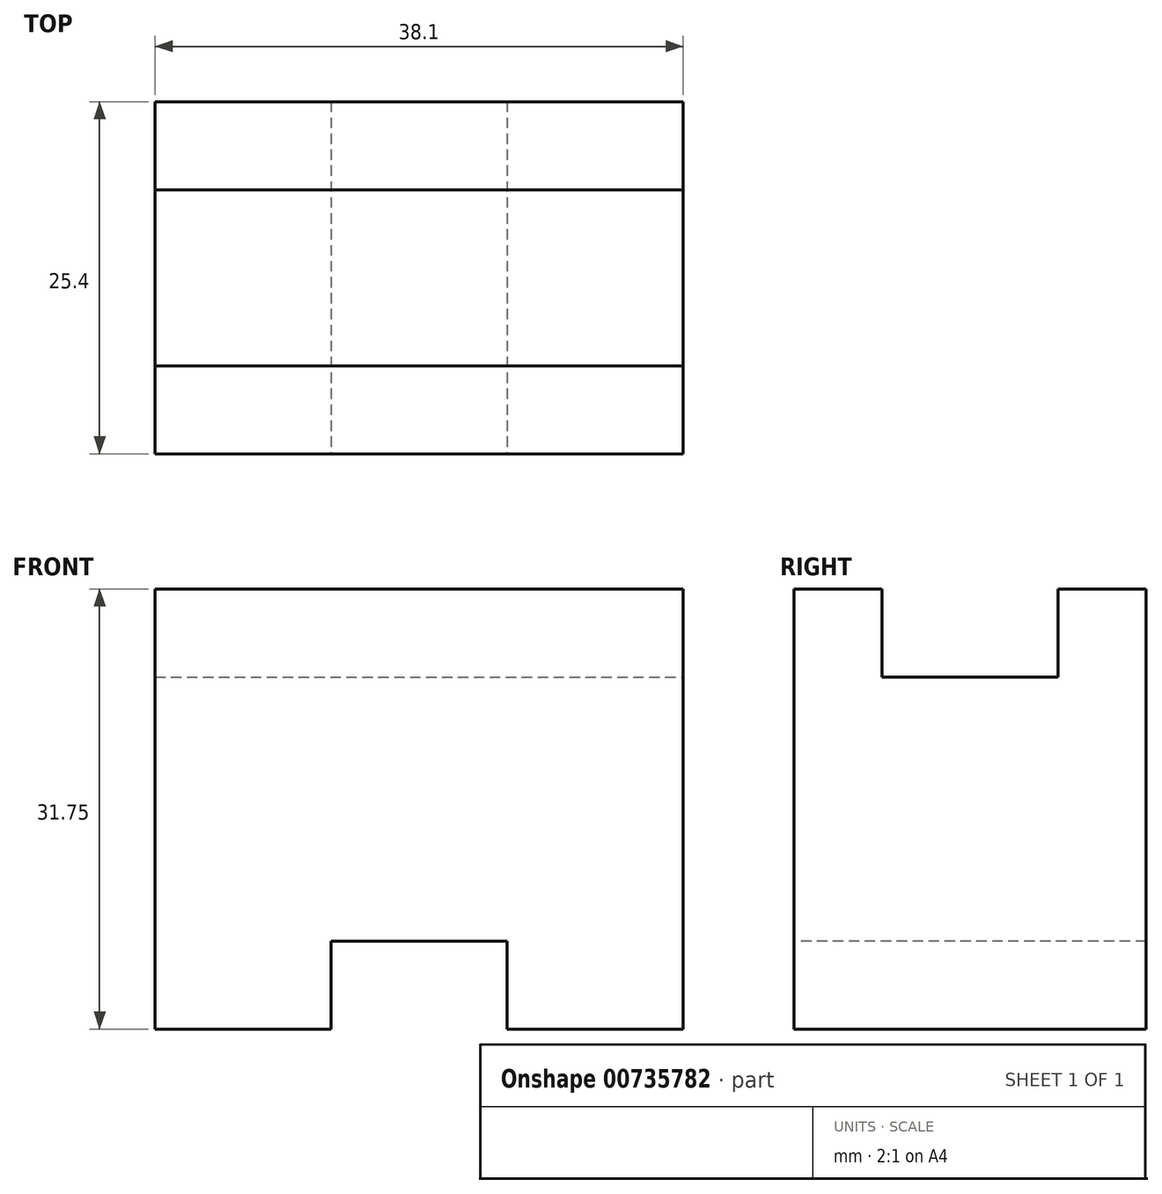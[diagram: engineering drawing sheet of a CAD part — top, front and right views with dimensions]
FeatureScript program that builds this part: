
annotation { "Feature Type Name" : "Feature", "Feature Type Description" : "" }
export const myFeature = defineFeature(function(context is Context, id is Id, definition is map)
    precondition{}
    {
        {
            var Q0;
            Q0=qCreatedBy(makeId("Front.planeOp"),FACE);
            var sketch = newSketch(context, id + "F0", { "sketchPlane" : qUnion([Q0])});
            skLineSegment(sketch, "E0", {"start": v(0, 0) * mm, "end": v(38.1, 0) * mm});
            skLineSegment(sketch, "E1", {"start": v(38.1, 0) * mm, "end": v(38.1, 31.75) * mm});
            skLineSegment(sketch, "E2", {"start": v(38.1, 31.75) * mm, "end": v(0, 31.75) * mm});
            skLineSegment(sketch, "E3", {"start": v(0, 31.75) * mm, "end": v(0, 0) * mm});
            skSolve(sketch);
        }
        {
            var Q0;
            Q0=makeQuery(id+"F0.imprint","IMPRINT",FACE,{"disambiguationData":[TD([[makeQuery(id+"F0.imprint","IMPRINT",EDGE,{"derivedFrom":sQuery(id+"F0.wireOp",EDGE,"E0")}),1.0]])]});
            extrude(context, id + "F1", {"entities" : qUnion([Q0]), "depth" : 25.4 * mm, "offsetDistance" : 25.4 * mm});
        }
        {
            var Q0;
            Q0=makeQuery(id+"F1.opExtrude","CAP_FACE",FACE,{"disambiguationData":[OSD([sQuery(id+"F0.wireOp",EDGE,"E0"),sQuery(id+"F0.wireOp",EDGE,"E1"),sQuery(id+"F0.wireOp",EDGE,"E2"),sQuery(id+"F0.wireOp",EDGE,"E3")])],"isStart":false});
            var sketch = newSketch(context, id + "F2", { "sketchPlane" : qUnion([Q0])});
            skLineSegment(sketch, "E4.bottom", {"start": v(12.7, 0) * mm, "end": v(25.4, 0) * mm});
            skLineSegment(sketch, "E4.top", {"start": v(12.7, 6.35) * mm, "end": v(25.4, 6.35) * mm});
            skLineSegment(sketch, "E4.left", {"start": v(12.7, 0) * mm, "end": v(12.7, 6.35) * mm});
            skLineSegment(sketch, "E4.right", {"start": v(25.4, 0) * mm, "end": v(25.4, 6.35) * mm});
            skLineSegment(sketch, "E5.bottom", {"start": v(38.1, 0) * mm, "end": v(25.4, 0) * mm});
            skLineSegment(sketch, "E5.top", {"start": v(38.1, 0) * mm, "end": v(25.4, 0) * mm});
            skLineSegment(sketch, "E5.left", {"start": v(38.1, 0) * mm, "end": v(38.1, 0) * mm});
            skLineSegment(sketch, "E5.right", {"start": v(25.4, 0) * mm, "end": v(25.4, 0) * mm});
            skSolve(sketch);
        }
        {
            var Q0;
            Q0 = qSketchRegion(id + "F2", true);
            extrude(context, id + "F3", {"entities" : qUnion([Q0]), "operationType" : NewBodyOperationType.REMOVE, "oppositeDirection" : true, "depth" : 25.4 * mm, "offsetDistance" : 25.4 * mm});
        }
        {
            var Q0;
            Q0=makeQuery(id+"F1.opExtrude","SWEPT_FACE",FACE,{"disambiguationData":[OSD([sQuery(id+"F0.wireOp",EDGE,"E2")])]});
            var sketch = newSketch(context, id + "F4", { "sketchPlane" : qUnion([Q0])});
            skLineSegment(sketch, "E6.bottom", {"start": v(0, -6.35) * mm, "end": v(38.1, -6.35) * mm});
            skLineSegment(sketch, "E6.top", {"start": v(0, -19.05) * mm, "end": v(38.1, -19.05) * mm});
            skLineSegment(sketch, "E6.left", {"start": v(0, -6.35) * mm, "end": v(0, -19.05) * mm});
            skLineSegment(sketch, "E6.right", {"start": v(38.1, -6.35) * mm, "end": v(38.1, -19.05) * mm});
            skSolve(sketch);
        }
        {
            var Q0;
            Q0=makeQuery(id+"F4.imprint","IMPRINT",FACE,{"disambiguationData":[TD([[makeQuery(id+"F4.imprint","IMPRINT",EDGE,{"derivedFrom":sQuery(id+"F4.wireOp",EDGE,"E6.bottom")}),-1.0]])]});
            extrude(context, id + "F5", {"entities" : qUnion([Q0]), "operationType" : NewBodyOperationType.REMOVE, "oppositeDirection" : true, "depth" : 6.35 * mm, "offsetDistance" : 25.4 * mm});
        }
    });
